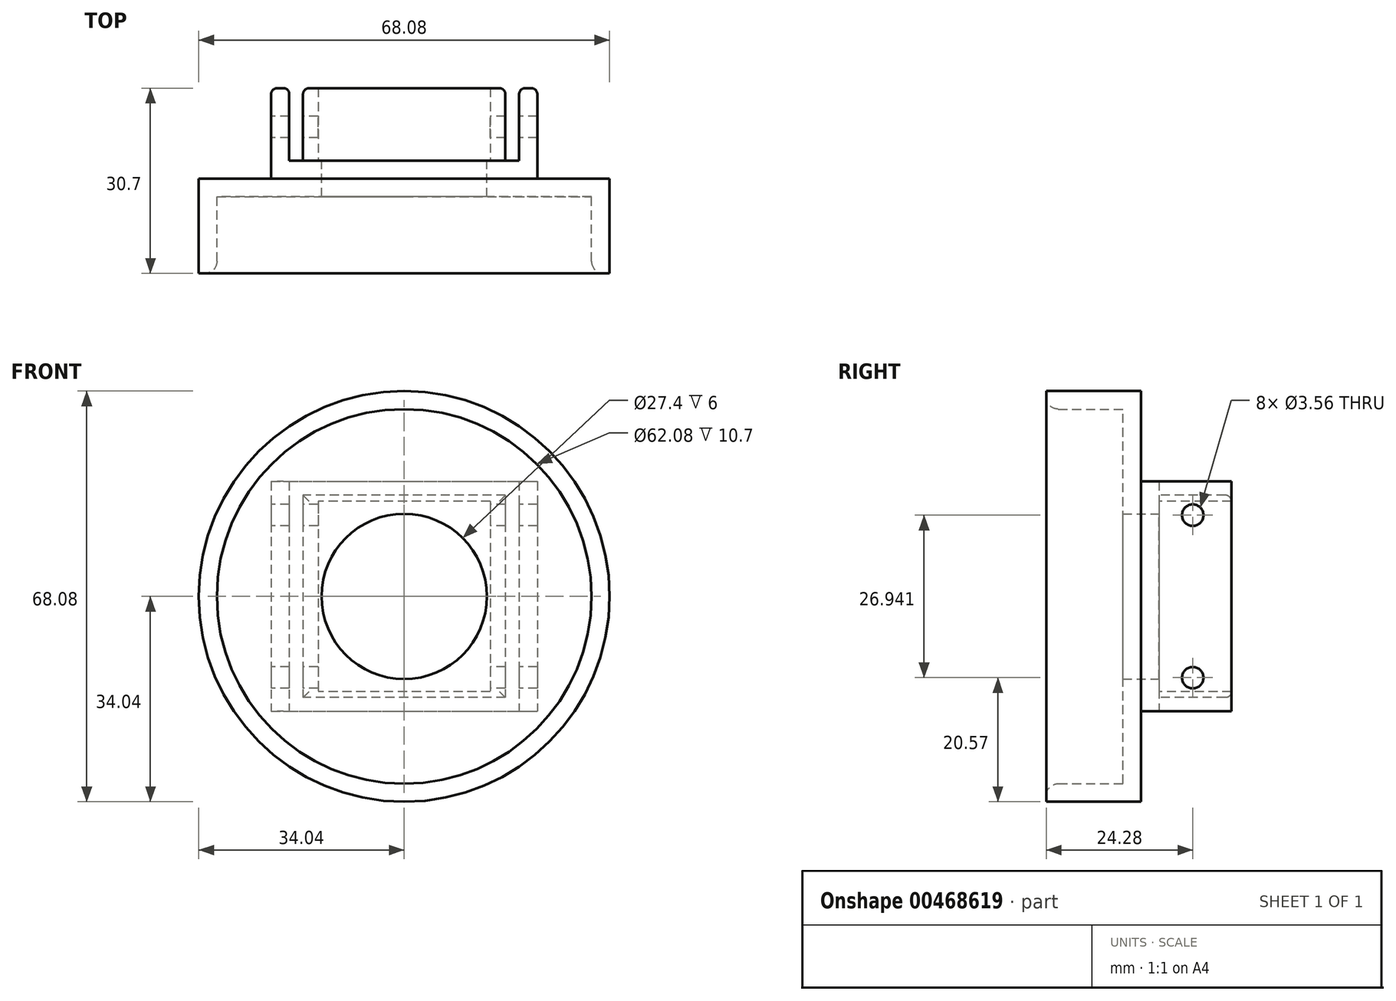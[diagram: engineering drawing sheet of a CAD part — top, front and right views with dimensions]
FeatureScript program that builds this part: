
annotation { "Feature Type Name" : "Feature", "Feature Type Description" : "" }
export const myFeature = defineFeature(function(context is Context, id is Id, definition is map)
    precondition{}
    {
        {
            var Q0;
            Q0=qCreatedBy(makeId("Front.planeOp"),FACE);
            var sketch = newSketch(context, id + "F0", { "sketchPlane" : qUnion([Q0])});
            skCircle(sketch, "E0", {"center": v(0, 0) * mm, "radius": 31.04 * mm});
            skCircle(sketch, "E1", {"center": v(0, 0) * mm, "radius": 34.04 * mm});
            skLineSegment(sketch, "E2.bottom", {"start": v(-19.05, 19.05) * mm, "end": v(19.05, 19.05) * mm});
            skLineSegment(sketch, "E2.top", {"start": v(-19.05, -19.05) * mm, "end": v(19.05, -19.05) * mm});
            skLineSegment(sketch, "E2.left", {"start": v(-19.05, 19.05) * mm, "end": v(-19.05, -19.05) * mm});
            skLineSegment(sketch, "E2.right", {"start": v(19.05, 19.05) * mm, "end": v(19.05, -19.05) * mm});
            skCircle(sketch, "E3", {"center": v(0, 0) * mm, "radius": 13.7 * mm});
            skSolve(sketch);
        }
        {
            var Q0;
            Q0=makeQuery(id+"F0.imprint","IMPRINT",FACE,{"disambiguationData":[TD([[makeQuery(id+"F0.imprint","IMPRINT",EDGE,{"derivedFrom":sQuery(id+"F0.wireOp",EDGE,"E0")}),-1.0]])]});
            var Q1;
            {var subQ1=sQuery(id+"F0.wireOp",EDGE,"0R0oGFEA-m8pK-yiVm-rlpr-hWKj9PhfM7ot.right");Q1=makeQuery(id+"F0.imprint","IMPRINT",FACE,{"disambiguationData":[TD([[makeQuery(id+"F0.imprint","IMPRINT",EDGE,{"derivedFrom":subQ1}),1.0]])]});}
            var Q2;
            {var subQ1=sQuery(id+"F0.wireOp",EDGE,"0R0oGFEA-m8pK-yiVm-rlpr-hWKj9PhfM7ot.left");Q2=makeQuery(id+"F0.imprint","IMPRINT",FACE,{"disambiguationData":[TD([[makeQuery(id+"F0.imprint","IMPRINT",EDGE,{"derivedFrom":subQ1}),-1.0]])]});}
            var Q3;
            {var subQ1=sQuery(id+"F0.wireOp",EDGE,"0R0oGFEA-m8pK-yiVm-rlpr-hWKj9PhfM7ot.bottom");var subQ3=sQuery(id+"F0.wireOp",EDGE,"E1");var subQ4=makeQuery(id+"F0.imprint","INTERSECT",VERTEX,{"derivedFrom":[subQ1,subQ3]});Q3=makeQuery(id+"F0.imprint","IMPRINT",FACE,{"disambiguationData":[TD([[makeQuery(id+"F0.imprint","IMPRINT",EDGE,{"disambiguationData":[TD([[subQ4,-1.0]])],"derivedFrom":subQ3}),-1.0]])]});}
            var Q4;
            {var subQ0=sQuery(id+"F0.wireOp",EDGE,"E1");var subQ1=sQuery(id+"F0.wireOp",EDGE,"0R0oGFEA-m8pK-yiVm-rlpr-hWKj9PhfM7ot.left");var subQ2=makeQuery(id+"F0.imprint","INTERSECT",VERTEX,{"disambiguationData":[OD(0.0)],"derivedFrom":[subQ1,subQ0]});Q4=makeQuery(id+"F0.imprint","IMPRINT",FACE,{"disambiguationData":[TD([[makeQuery(id+"F0.imprint","IMPRINT",EDGE,{"disambiguationData":[TD([[subQ2,-1.0]])],"derivedFrom":subQ1}),-1.0]])]});}
            var Q5;
            {var subQ0=sQuery(id+"F0.wireOp",EDGE,"E1");var subQ1=sQuery(id+"F0.wireOp",EDGE,"0R0oGFEA-m8pK-yiVm-rlpr-hWKj9PhfM7ot.right");var subQ2=makeQuery(id+"F0.imprint","INTERSECT",VERTEX,{"disambiguationData":[OD(0.0)],"derivedFrom":[subQ1,subQ0]});Q5=makeQuery(id+"F0.imprint","IMPRINT",FACE,{"disambiguationData":[TD([[makeQuery(id+"F0.imprint","IMPRINT",EDGE,{"disambiguationData":[TD([[subQ2,-1.0]])],"derivedFrom":subQ1}),1.0]])]});}
            var Q6;
            {var subQ1=sQuery(id+"F0.wireOp",EDGE,"0R0oGFEA-m8pK-yiVm-rlpr-hWKj9PhfM7ot.bottom");var subQ3=sQuery(id+"F0.wireOp",EDGE,"E1");var subQ4=makeQuery(id+"F0.imprint","INTERSECT",VERTEX,{"derivedFrom":[subQ1,subQ3]});Q6=makeQuery(id+"F0.imprint","IMPRINT",FACE,{"disambiguationData":[TD([[makeQuery(id+"F0.imprint","IMPRINT",EDGE,{"disambiguationData":[TD([[subQ4,1.0]])],"derivedFrom":subQ3}),-1.0]])]});}
            var Q7;
            {var subQ1=sQuery(id+"F0.wireOp",EDGE,"0R0oGFEA-m8pK-yiVm-rlpr-hWKj9PhfM7ot.top");var subQ3=sQuery(id+"F0.wireOp",EDGE,"E1");var subQ4=makeQuery(id+"F0.imprint","INTERSECT",VERTEX,{"derivedFrom":[subQ1,subQ3]});Q7=makeQuery(id+"F0.imprint","IMPRINT",FACE,{"disambiguationData":[TD([[makeQuery(id+"F0.imprint","IMPRINT",EDGE,{"disambiguationData":[TD([[subQ4,-1.0]])],"derivedFrom":subQ3}),-1.0]])]});}
            var Q8;
            {var subQ1=sQuery(id+"F0.wireOp",EDGE,"0R0oGFEA-m8pK-yiVm-rlpr-hWKj9PhfM7ot.top");var subQ3=sQuery(id+"F0.wireOp",EDGE,"E1");var subQ4=makeQuery(id+"F0.imprint","INTERSECT",VERTEX,{"derivedFrom":[subQ1,subQ3]});Q8=makeQuery(id+"F0.imprint","IMPRINT",FACE,{"disambiguationData":[TD([[makeQuery(id+"F0.imprint","IMPRINT",EDGE,{"disambiguationData":[TD([[subQ4,1.0]])],"derivedFrom":subQ3}),-1.0]])]});}
            var Q9;
            Q9=makeQuery(id+"F0.imprint","IMPRINT",FACE,{"disambiguationData":[TD([[makeQuery(id+"F0.imprint","IMPRINT",EDGE,{"derivedFrom":sQuery(id+"F0.wireOp",EDGE,"E0")}),1.0]])]});
            var Q10;
            Q10=makeQuery(id+"F0.imprint","IMPRINT",FACE,{"disambiguationData":[TD([[makeQuery(id+"F0.imprint","IMPRINT",EDGE,{"derivedFrom":sQuery(id+"F0.wireOp",EDGE,"E2.bottom")}),-1.0]])]});
            extrude(context, id + "F1", {"entities" : qUnion([Q0, Q1, Q2, Q3, Q4, Q5, Q6, Q7, Q8, Q9, Q10]), "depth" : 3 * mm, "offsetDistance" : 25 * mm});
        }
        {
            var Q0;
            Q0=makeQuery(id+"F0.imprint","IMPRINT",FACE,{"disambiguationData":[TD([[makeQuery(id+"F0.imprint","IMPRINT",EDGE,{"derivedFrom":sQuery(id+"F0.wireOp",EDGE,"E2.bottom")}),-1.0]])]});
            extrude(context, id + "F2", {"entities" : qUnion([Q0]), "operationType" : NewBodyOperationType.ADD, "oppositeDirection" : true, "depth" : 3 * mm, "offsetDistance" : 25 * mm});
        }
        {
            var Q0;
            Q0=makeQuery(id+"F0.imprint","IMPRINT",FACE,{"disambiguationData":[TD([[makeQuery(id+"F0.imprint","IMPRINT",EDGE,{"derivedFrom":sQuery(id+"F0.wireOp",EDGE,"E0")}),-1.0]])]});
            extrude(context, id + "F3", {"entities" : qUnion([Q0]), "operationType" : NewBodyOperationType.ADD, "depth" : 12.7 * mm + 3 * mm, "offsetDistance" : 25 * mm});
        }
        {
            var Q0;
            Q0=makeQuery(id+"F3.opExtrude","CAP_EDGE",EDGE,{"disambiguationData":[OSD([sQuery(id+"F0.wireOp",EDGE,"E0")])],"isStart":false});
            fillet(context, id + "F4", {"entities" : qUnion([Q0]), "radius" : 2 * mm, "tangentPropagation" : true, "allowEdgeOverflow" : false});
        }
        {
            var Q0;
            Q0=qCreatedBy(makeId("Front.planeOp"),FACE);
            var sketch = newSketch(context, id + "F5", { "sketchPlane" : qUnion([Q0])});
            skLineSegment(sketch, "E4.bottom", {"start": v(19.05, 19.05) * mm, "end": v(-19.05, 19.05) * mm});
            skLineSegment(sketch, "E4.top", {"start": v(19.05, -19.05) * mm, "end": v(-19.05, -19.05) * mm});
            skLineSegment(sketch, "E4.left", {"start": v(19.05, 19.05) * mm, "end": v(19.05, -19.05) * mm});
            skLineSegment(sketch, "E4.right", {"start": v(-19.05, 19.05) * mm, "end": v(-19.05, -19.05) * mm});
            skPoint(sketch, "E4.middle", {"position": v(0, 0) * mm});
            skLineSegment(sketch, "E5.bottom", {"start": v(19.05, 19.05) * mm, "end": v(22.05, 19.05) * mm});
            skLineSegment(sketch, "E5.top", {"start": v(19.05, -19.05) * mm, "end": v(22.05, -19.05) * mm});
            skLineSegment(sketch, "E5.right", {"start": v(22.05, 19.05) * mm, "end": v(22.05, -19.05) * mm});
            skLineSegment(sketch, "E6.bottom", {"start": v(-19.05, 19.05) * mm, "end": v(-22.05, 19.05) * mm});
            skLineSegment(sketch, "E6.top", {"start": v(-19.05, -19.05) * mm, "end": v(-22.05, -19.05) * mm});
            skLineSegment(sketch, "E6.right", {"start": v(-22.05, 19.05) * mm, "end": v(-22.05, -19.05) * mm});
            skLineSegment(sketch, "E7.bottom", {"start": v(16.76, 16.76) * mm, "end": v(-16.76, 16.76) * mm});
            skLineSegment(sketch, "E7.top", {"start": v(16.76, -16.76) * mm, "end": v(-16.76, -16.76) * mm});
            skLineSegment(sketch, "E7.left", {"start": v(16.76, 16.76) * mm, "end": v(16.76, -16.76) * mm});
            skLineSegment(sketch, "E7.right", {"start": v(-16.76, 16.76) * mm, "end": v(-16.76, -16.76) * mm});
            skLineSegment(sketch, "E8.bottom", {"start": v(14.26, 15.76) * mm, "end": v(-14.26, 15.76) * mm});
            skLineSegment(sketch, "E8.top", {"start": v(14.26, -15.76) * mm, "end": v(-14.26, -15.76) * mm});
            skLineSegment(sketch, "E8.left", {"start": v(14.26, 15.76) * mm, "end": v(14.26, -15.76) * mm});
            skLineSegment(sketch, "E8.right", {"start": v(-14.26, 15.76) * mm, "end": v(-14.26, -15.76) * mm});
            skSolve(sketch);
        }
        {
            var Q0;
            Q0=makeQuery(id+"F5.imprint","IMPRINT",FACE,{"disambiguationData":[TD([[makeQuery(id+"F5.imprint","IMPRINT",EDGE,{"derivedFrom":sQuery(id+"F5.wireOp",EDGE,"E4.right")}),-1.0]])]});
            var Q1;
            Q1=makeQuery(id+"F5.imprint","IMPRINT",FACE,{"disambiguationData":[TD([[makeQuery(id+"F5.imprint","IMPRINT",EDGE,{"derivedFrom":sQuery(id+"F5.wireOp",EDGE,"E4.left")}),1.0]])]});
            var Q2;
            Q2=makeQuery(id+"F5.imprint","IMPRINT",FACE,{"disambiguationData":[TD([[makeQuery(id+"F5.imprint","IMPRINT",EDGE,{"derivedFrom":sQuery(id+"F5.wireOp",EDGE,"E7.bottom")}),1.0]])]});
            extrude(context, id + "F6", {"entities" : qUnion([Q0, Q1, Q2]), "operationType" : NewBodyOperationType.ADD, "oppositeDirection" : true, "depth" : 15 * mm, "offsetDistance" : 25 * mm});
        }
        {
            var Q0;
            Q0=makeQuery(id+"F6.opExtrude","CAP_EDGE",EDGE,{"disambiguationData":[OSD([sQuery(id+"F5.wireOp",EDGE,"E4.right")])],"isStart":false});
            var Q1;
            Q1=makeQuery(id+"F6.opExtrude","CAP_EDGE",EDGE,{"disambiguationData":[OSD([sQuery(id+"F5.wireOp",EDGE,"E7.right")])],"isStart":false});
            var Q2;
            Q2=makeQuery(id+"F6.opExtrude","CAP_EDGE",EDGE,{"disambiguationData":[OSD([sQuery(id+"F5.wireOp",EDGE,"E4.left")])],"isStart":false});
            var Q3;
            Q3=makeQuery(id+"F6.opExtrude","CAP_EDGE",EDGE,{"disambiguationData":[OSD([sQuery(id+"F5.wireOp",EDGE,"E7.left")])],"isStart":false});
            var Q4;
            Q4=makeQuery(id+"F6.opExtrude","CAP_EDGE",EDGE,{"disambiguationData":[OSD([sQuery(id+"F5.wireOp",EDGE,"E7.bottom")])],"isStart":false});
            var Q5;
            Q5=makeQuery(id+"F6.opExtrude","CAP_EDGE",EDGE,{"disambiguationData":[OSD([sQuery(id+"F5.wireOp",EDGE,"E7.top")])],"isStart":false});
            var Q6;
            Q6=makeQuery(id+"F6.opExtrude","CAP_EDGE",EDGE,{"disambiguationData":[OSD([sQuery(id+"F5.wireOp",EDGE,"E5.right")])],"isStart":false});
            var Q7;
            Q7=makeQuery(id+"F6.opExtrude","CAP_EDGE",EDGE,{"disambiguationData":[OSD([sQuery(id+"F5.wireOp",EDGE,"E6.right")])],"isStart":false});
            fillet(context, id + "F7", {"entities" : qUnion([Q0, Q1, Q2, Q3, Q4, Q5, Q6, Q7]), "tangentPropagation" : true, "radius" : 1 * mm, "defaultsChanged" : false, "vertexSettings" : [], "allowEdgeOverflow" : false});
        }
        {
            var Q0;
            Q0=makeQuery(id+"F6.opExtrude","SWEPT_FACE",FACE,{"disambiguationData":[OSD([sQuery(id+"F5.wireOp",EDGE,"E6.right")])]});
            var sketch = newSketch(context, id + "F8", { "sketchPlane" : qUnion([Q0])});
            skLineSegment(sketch, "E9.bottom", {"start": v(0, 19.05) * mm, "end": v(-3, 19.05) * mm});
            skLineSegment(sketch, "E9.top", {"start": v(0, -19.05) * mm, "end": v(-3, -19.05) * mm});
            skLineSegment(sketch, "E9.left", {"start": v(0, 19.05) * mm, "end": v(0, -19.05) * mm});
            skLineSegment(sketch, "E9.right", {"start": v(-3, 19.05) * mm, "end": v(-3, -19.05) * mm, "construction": true});
            skCircle(sketch, "E10", {"center": v(-22.05, 0) * mm, "radius": 19.05 * mm, "construction": true});
            skLineSegment(sketch, "E11.bottom", {"start": v(-35.52, 13.47) * mm, "end": v(-8.58, 13.47) * mm, "construction": true});
            skLineSegment(sketch, "E11.top", {"start": v(-35.52, -13.47) * mm, "end": v(-8.58, -13.47) * mm, "construction": true});
            skLineSegment(sketch, "E11.left", {"start": v(-35.52, 13.47) * mm, "end": v(-35.52, -13.47) * mm, "construction": true});
            skLineSegment(sketch, "E11.right", {"start": v(-8.58, 13.47) * mm, "end": v(-8.58, -13.47) * mm, "construction": true});
            skCircle(sketch, "E12", {"center": v(-8.58, 13.47) * mm, "radius": 1.78 * mm});
            skCircle(sketch, "E13", {"center": v(-8.58, -13.47) * mm, "radius": 1.78 * mm});
            skSolve(sketch);
        }
        {
            var Q0;
            Q0=makeQuery(id+"F8.imprint","IMPRINT",FACE,{"disambiguationData":[TD([[makeQuery(id+"F8.imprint","IMPRINT",EDGE,{"derivedFrom":sQuery(id+"F8.wireOp",EDGE,"E12")}),1.0]])]});
            var Q1;
            Q1=makeQuery(id+"F8.imprint","IMPRINT",FACE,{"disambiguationData":[TD([[makeQuery(id+"F8.imprint","IMPRINT",EDGE,{"derivedFrom":sQuery(id+"F8.wireOp",EDGE,"E13")}),1.0]])]});
            var Q2;
            Q2=sQuery(id+"F8.wireOp",EDGE,"E12");
            var Q3;
            Q3=sQuery(id+"F8.wireOp",EDGE,"E13");
            extrude(context, id + "F9", {"entities" : qUnion([Q0, Q1]), "operationType" : NewBodyOperationType.REMOVE, "surfaceEntities" : qUnion([Q2, Q3]), "endBound" : BoundingType.THROUGH_ALL, "oppositeDirection" : true, "depth" : 25 * mm, "offsetDistance" : 25 * mm});
        }
    });
